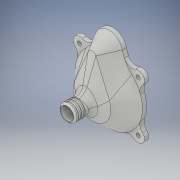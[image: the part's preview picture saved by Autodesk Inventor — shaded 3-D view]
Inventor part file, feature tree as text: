
AUTODESK INVENTOR PART (.ipt)
format: ipt  version: 2018 (Build 220112000, 112)  size: 827,904 bytes
history: native  units: in
note: dims shown in document units (in); Inventor stores cm internally (conversion verified against a paired STEP export)
features: sketch x7, plane x5, extrude x5, fillet x4, projected_geometry x3, loft x2, shell x2, mirror x1, pattern_linear x1, chamfer x1, other x1
ambient origin geometry x8: Origin, YZ Plane, XZ Plane, XY Plane, X Axis, Y Axis, Z Axis, Center Point
bodies: Body1 (feature_tree)
feature tree (32):
  sketch  "Sketch2"  dims[d4=4.0in d5=0.825in]
  plane  "Work Plane2"
  loft  "Loft2"
  extrude  "Extrusion1"  Depth=2.0in
  plane  "Work Plane5"
  loft  "Loft6"
  shell  "Shell3"  Thickness=1.125in
  sketch  "Sketch20"  dims[d25=0.25in d26=0.0in d41=0.1in d42=0.75in d55=0.5in]
  extrude  "Extrusion4"  TaperAngle=0.0deg  [1 undecoded]
  extrude  "Extrusion5"  Depth=0.1in
  fillet  "Fillet3"  Radius=0.75in
  fillet  "Fillet4"  Radius=0.5in
  extrude  "Extrusion6"  TaperAngle=0.0deg  [1 undecoded]
  fillet  "Fillet5"  [1 undecoded]
  mirror  "Mirror1"
  fillet  "Fillet6"  Radius=0.1in
  plane  "Work Plane6"
  extrude  "Extrusion7"  Depth=0.1in TaperAngle=0.0deg
  pattern_linear  "Rectangular Pattern1"  Spacing1=1.0in  [1 undecoded]
  chamfer  "Chamfer1"  Distance=0.5in
  shell  "Shell1"  Thickness=0.5in
  plane  "Work Plane3"
  plane  "Work Plane4"
  sketch  "Sketch7"  dims[d6=2.25in d7=2.0in]
  sketch  "Sketch8"  dims[d18=1.0in d19=0.25in d20=1.125in]
  projected_geometry  "Projected Loop1"
  sketch  "Sketch19"  dims[d21=0.0in d22=90.0deg d23=0.0in d24=90.0deg]
  other  "Edges6"
  projected_geometry  "Projected Loop6"
  sketch  "Sketch21"  dims[d56=1.0in d57=0.0in d58=90.0deg d59=0.0in d60=90.0deg d61=0.1in]
  projected_geometry  "Projected Loop7"
  sketch  "Sketch22"  dims[d63=0.125in d64=1.0in d65=0.0in d66=1.0in d67=0.0in d68=0.5in d69=0.5in d70=1.75in d71=1.5in d72=1.75in d73=1.5in d74=0.25in d75=0.25in d76=0.25in d77=0.0in d78=0.5in d79=0.5in d80=-0.1in d81=0.95in d82=0.1in d83=0.0in d84=1.1811in d86=0.2in d87=0.1in d88=0.125in d89=45.0deg]
note: 4 required parameter values undecoded (feature->parameter linkage not recoverable at this tier; creation-order binding heuristic only, values carry confidence <= 0.55)
